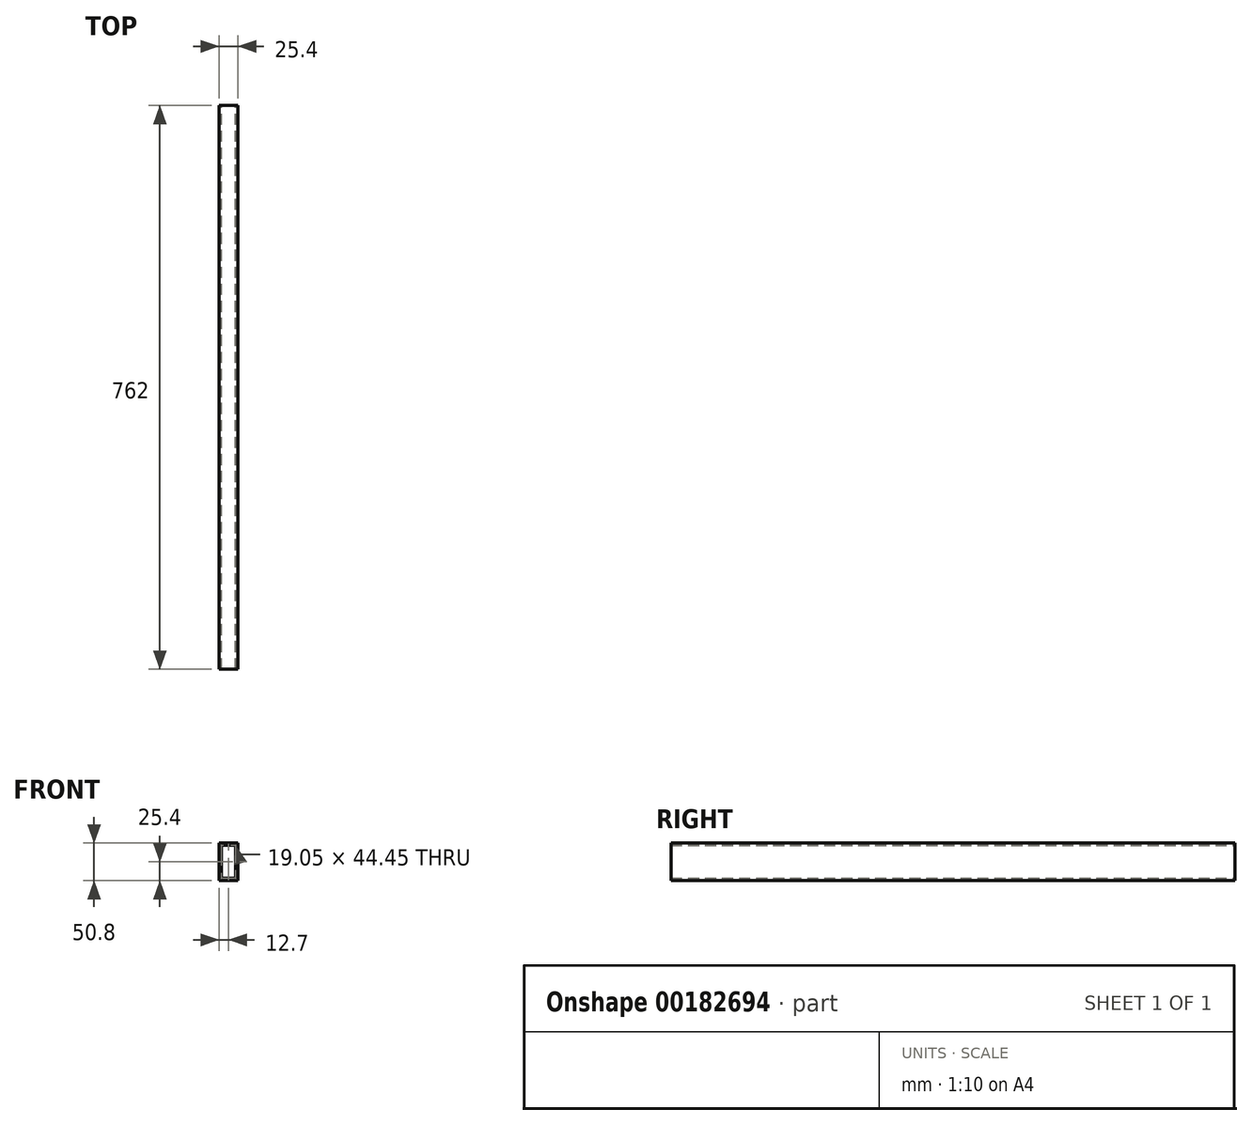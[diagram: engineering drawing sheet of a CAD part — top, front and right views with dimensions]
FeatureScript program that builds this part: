
annotation { "Feature Type Name" : "Feature", "Feature Type Description" : "" }
export const myFeature = defineFeature(function(context is Context, id is Id, definition is map)
    precondition{}
    {
        {
            var Q0;
            Q0=qCreatedBy(makeId("Front.planeOp"),FACE);
            var sketch = newSketch(context, id + "F0", { "sketchPlane" : qUnion([Q0])});
            skLineSegment(sketch, "E0.bottom", {"start": v(0, 0) * mm, "end": v(25.4, 0) * mm});
            skLineSegment(sketch, "E0.top", {"start": v(0, 50.8) * mm, "end": v(25.4, 50.8) * mm});
            skLineSegment(sketch, "E0.left", {"start": v(0, 0) * mm, "end": v(0, 50.8) * mm});
            skLineSegment(sketch, "E0.right", {"start": v(25.4, 0) * mm, "end": v(25.4, 50.8) * mm});
            skLineSegment(sketch, "E1.0", {"start": v(22.23, 3.18) * mm, "end": v(22.22, 47.62) * mm});
            skLineSegment(sketch, "E1.1", {"start": v(3.18, 3.18) * mm, "end": v(22.23, 3.18) * mm});
            skLineSegment(sketch, "E1.2", {"start": v(3.18, 3.18) * mm, "end": v(3.17, 47.62) * mm});
            skLineSegment(sketch, "E1.3", {"start": v(3.17, 47.62) * mm, "end": v(22.22, 47.62) * mm});
            skSolve(sketch);
        }
        {
            var Q0;
            Q0=makeQuery(id+"F0.imprint","IMPRINT",FACE,{"disambiguationData":[TD([[makeQuery(id+"F0.imprint","IMPRINT",EDGE,{"derivedFrom":sQuery(id+"F0.wireOp",EDGE,"E0.bottom")}),1.0]])]});
            extrude(context, id + "F1", {"entities" : qUnion([Q0]), "depth" : 762 * mm});
        }
    });
